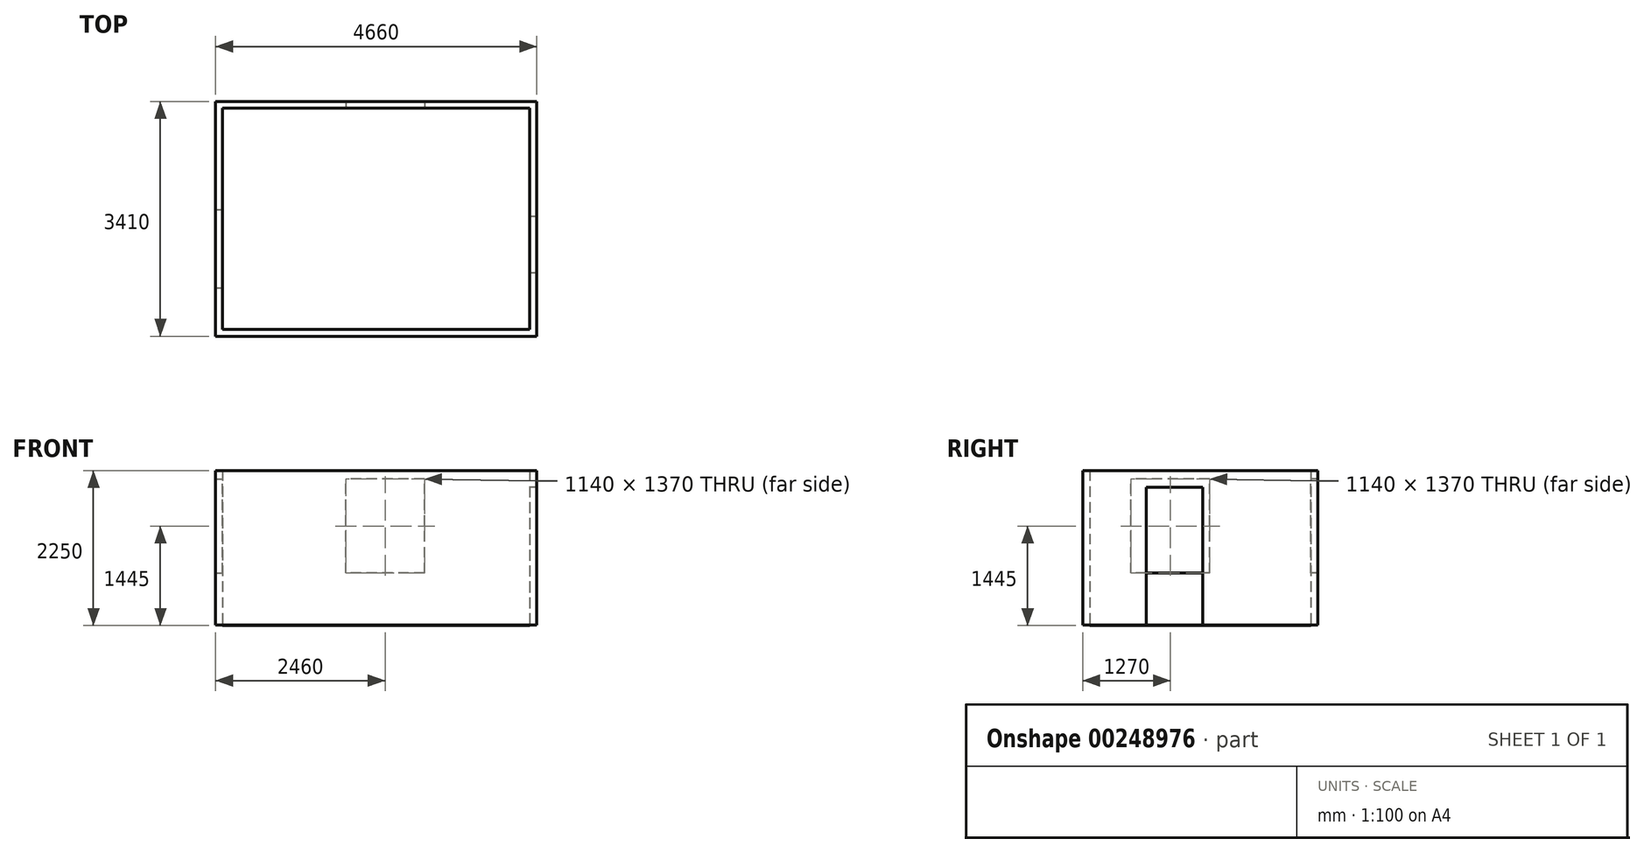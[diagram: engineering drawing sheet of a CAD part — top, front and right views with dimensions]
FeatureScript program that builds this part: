
annotation { "Feature Type Name" : "Feature", "Feature Type Description" : "" }
export const myFeature = defineFeature(function(context is Context, id is Id, definition is map)
    precondition{}
    {
        {
            var Q0;
            Q0=qCreatedBy(makeId("Top.planeOp"),FACE);
            var sketch = newSketch(context, id + "F0", { "sketchPlane" : qUnion([Q0])});
            skLineSegment(sketch, "E0.bottom", {"start": v(2230, 1605) * mm, "end": v(-2230, 1605) * mm});
            skLineSegment(sketch, "E0.top", {"start": v(2230, -1605) * mm, "end": v(-2230, -1605) * mm});
            skLineSegment(sketch, "E0.left", {"start": v(2230, 1605) * mm, "end": v(2230, -1605) * mm});
            skLineSegment(sketch, "E0.right", {"start": v(-2230, 1605) * mm, "end": v(-2230, -1605) * mm});
            skPoint(sketch, "E0.middle", {"position": v(0, 0) * mm});
            skSolve(sketch);
        }
        {
            var Q0;
            Q0 = qSketchRegion(id + "F0", true);
            extrude(context, id + "F1", {"entities" : qUnion([Q0]), "depth" : 10 * mm});
        }
        {
            var Q0;
            Q0=makeQuery(id+"F1.opExtrude","CAP_FACE",FACE,{"disambiguationData":[OSD([sQuery(id+"F0.wireOp",EDGE,"E0.bottom"),sQuery(id+"F0.wireOp",EDGE,"E0.top"),sQuery(id+"F0.wireOp",EDGE,"E0.left"),sQuery(id+"F0.wireOp",EDGE,"E0.right")])],"isStart":false});
            var sketch = newSketch(context, id + "F2", { "sketchPlane" : qUnion([Q0])});
            skLineSegment(sketch, "E1.bottom", {"start": v(2230, 1605) * mm, "end": v(-2230, 1605) * mm});
            skLineSegment(sketch, "E1.top", {"start": v(2230, -1605) * mm, "end": v(-2230, -1605) * mm});
            skLineSegment(sketch, "E1.left", {"start": v(2230, 1605) * mm, "end": v(2230, -1605) * mm});
            skLineSegment(sketch, "E1.right", {"start": v(-2230, 1605) * mm, "end": v(-2230, -1605) * mm});
            skPoint(sketch, "E1.middle", {"position": v(0, 0) * mm});
            skLineSegment(sketch, "E2.bottom", {"start": v(2330, 1705) * mm, "end": v(-2330, 1705) * mm});
            skLineSegment(sketch, "E2.top", {"start": v(2330, -1705) * mm, "end": v(-2330, -1705) * mm});
            skLineSegment(sketch, "E2.left", {"start": v(2330, 1705) * mm, "end": v(2330, -1705) * mm});
            skLineSegment(sketch, "E2.right", {"start": v(-2330, 1705) * mm, "end": v(-2330, -1705) * mm});
            skSolve(sketch);
        }
        {
            var Q0;
            Q0 = qSketchRegion(id + "F2", true);
            extrude(context, id + "F3", {"entities" : qUnion([Q0]), "operationType" : NewBodyOperationType.ADD, "depth" : 2240 * mm});
        }
        {
            var Q0;
            Q0=makeQuery(id+"F3.opExtrude","SWEPT_FACE",FACE,{"disambiguationData":[OSD([sQuery(id+"F2.wireOp",EDGE,"E1.right")])]});
            var sketch = newSketch(context, id + "F4", { "sketchPlane" : qUnion([Q0])});
            skLineSegment(sketch, "E3.bottom", {"start": v(135, 760) * mm, "end": v(-1005, 760) * mm});
            skLineSegment(sketch, "E3.top", {"start": v(135, 2130) * mm, "end": v(-1005, 2130) * mm});
            skLineSegment(sketch, "E3.left", {"start": v(135, 760) * mm, "end": v(135, 2130) * mm});
            skLineSegment(sketch, "E3.right", {"start": v(-1005, 760) * mm, "end": v(-1005, 2130) * mm});
            skPoint(sketch, "E3.middle", {"position": v(-435, 1445) * mm});
            skSolve(sketch);
        }
        {
            var Q0;
            Q0 = qSketchRegion(id + "F4", true);
            extrude(context, id + "F5", {"entities" : qUnion([Q0]), "operationType" : NewBodyOperationType.REMOVE, "oppositeDirection" : true, "depth" : 300 * mm});
        }
        {
            var Q0;
            Q0=makeQuery(id+"F3.opExtrude","SWEPT_FACE",FACE,{"disambiguationData":[OSD([sQuery(id+"F2.wireOp",EDGE,"E1.bottom")])]});
            var sketch = newSketch(context, id + "F6", { "sketchPlane" : qUnion([Q0])});
            skLineSegment(sketch, "E4.bottom", {"start": v(700, 760) * mm, "end": v(-440, 760) * mm});
            skLineSegment(sketch, "E4.top", {"start": v(700, 2130) * mm, "end": v(-440, 2130) * mm});
            skLineSegment(sketch, "E4.left", {"start": v(700, 760) * mm, "end": v(700, 2130) * mm});
            skLineSegment(sketch, "E4.right", {"start": v(-440, 760) * mm, "end": v(-440, 2130) * mm});
            skPoint(sketch, "E4.middle", {"position": v(130, 1445) * mm});
            skSolve(sketch);
        }
        {
            var Q0;
            Q0 = qSketchRegion(id + "F6", true);
            extrude(context, id + "F7", {"entities" : qUnion([Q0]), "operationType" : NewBodyOperationType.REMOVE, "oppositeDirection" : true, "depth" : 300 * mm});
        }
        {
            var Q0;
            Q0=makeQuery(id+"F3.opExtrude","SWEPT_FACE",FACE,{"disambiguationData":[OSD([sQuery(id+"F2.wireOp",EDGE,"E1.left")])]});
            var sketch = newSketch(context, id + "F8", { "sketchPlane" : qUnion([Q0])});
            skLineSegment(sketch, "E5.bottom", {"start": v(785, 2010) * mm, "end": v(-35, 2010) * mm});
            skLineSegment(sketch, "E5.top", {"start": v(785, 10) * mm, "end": v(-35, 10) * mm});
            skLineSegment(sketch, "E5.left", {"start": v(785, 2010) * mm, "end": v(785, 10) * mm});
            skLineSegment(sketch, "E5.right", {"start": v(-35, 2010) * mm, "end": v(-35, 10) * mm});
            skPoint(sketch, "E5.middle", {"position": v(375, 1010) * mm});
            skSolve(sketch);
        }
        {
            var Q0;
            Q0 = qSketchRegion(id + "F8", true);
            extrude(context, id + "F9", {"entities" : qUnion([Q0]), "operationType" : NewBodyOperationType.REMOVE, "oppositeDirection" : true, "depth" : 150 * mm});
        }
    });
